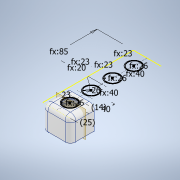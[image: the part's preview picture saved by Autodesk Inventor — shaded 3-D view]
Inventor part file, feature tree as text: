
AUTODESK INVENTOR PART (.ipt)
format: ipt  version: 2021 (Build 250183000, 183)  size: 1,942,528 bytes
history: native  units: in
note: dims shown in document units (in); Inventor stores cm internally (conversion verified against a paired STEP export)
features: extrude x10, other x9, fillet x3, sketch x1
ambient origin geometry x8: Origin, YZ Plane, XZ Plane, XY Plane, X Axis, Y Axis, Z Axis, Center Point
bodies: Body1 (feature_tree)
feature tree (23):
  extrude  "Base"  Depth=0.3937in
  other  "Top Indent Sketch"
  extrude  "Top"  Depth=0.3937in TaperAngle=0.0deg
  extrude  "Walls"  Depth=0.3937in
  fillet  "Outer"  Radius=1.0236in
  extrude  "Outer Wire"  Depth=0.3937in
  extrude  "Wall Holes"  Depth=0.3937in
  extrude  "Text"  Depth=0.3937in
  extrude  "Inner Sketch"  Depth=0.3937in
  fillet  "Inner Fillet"  Radius=1.5748in
  extrude  "Top Indent"  Depth=0.3937in TaperAngle=0.0deg
  other  "Wire Hole Plane"
  extrude  "Wire Hole"  Depth=0.3937in
  fillet  "Fillet10"  Radius=0.315in
  extrude  "Extrusion21"  Depth=0.3937in
  other  "Base Sketch"
  other  "Walls Sketch"
  other  "Outer Wire Sketch"
  other  "Wall Holes Sketch"
  other  "Text Sketch"
  other  "Inner Support Sketch"
  other  "Wire Hole Sketch"
  sketch  "Sketch31"  dims[d6=6.6929in d7=2.0472in d8=1.7717in d9=0.0in d10=1.0236in d11=1.0236in d12=1.0236in d13=1.0236in d14=1.5748in d15=1.5748in d16=1.5748in d19=0.7087in d20=0.0in d21=0.315in d22=0.315in d23=0.2362in d24=0.2362in d25=1.4567in d26=0.0in d27=0.9055in d28=0.9055in d29=0.9055in d30=0.9055in d31=0.7874in d32=3.3465in d33=1.5748in d35=0.9843in d36=0.3937in d38=0.3937in d39=0.0in d52=0.315in d55=0.1969in d56=0.0in d58=0.5512in d65=0.2362in d66=0.1575in d67=0.1181in d68=0.2362in d69=0.2774in d70=0.2774in d71=0.0499in d72=0.0499in d73=0.0787in d74=0.0in d77=0.6496in d81=0.9843in d82=0.0in d85=0.5906in d86=0.1575in d87=0.1575in d88=1.0236in d89=0.315in d90=0.1181in d92=0.0in d93=0.1181in d94=0.0in d95=0.1181in d96=0.6496in d143=0.0in d144=0.0in d158=0.0945in d159=0.0in d162=0.2362in d163=0.0in d164=0.0in d165=0.1969in d166=0.2362in d167=0.0in d168=0.1969in d169=0.1969in d170=4.7244in d171=0.0in d172=3.3465in d173=1.0236in d175=1.2992in d178=0.0787in d179=0.1969in d180=0.1969in d181=0.0in d182=0.0394in d194=4.9213in d195=0.0in d44=0.0197in d45=0.0344in d46=0.0197in d47=0.0344in d48=0.0197in d49=0.0344in d59=0.0197in d60=0.0344in d61=0.0197in d62=0.0344in d176=0.0344in d177=0.0197in d183=0.0197in d184=0.0344in d185=0.0197in d186=0.0344in d196=0.0197in d197=0.0344in d198=0.0197in d199=0.0344in]
